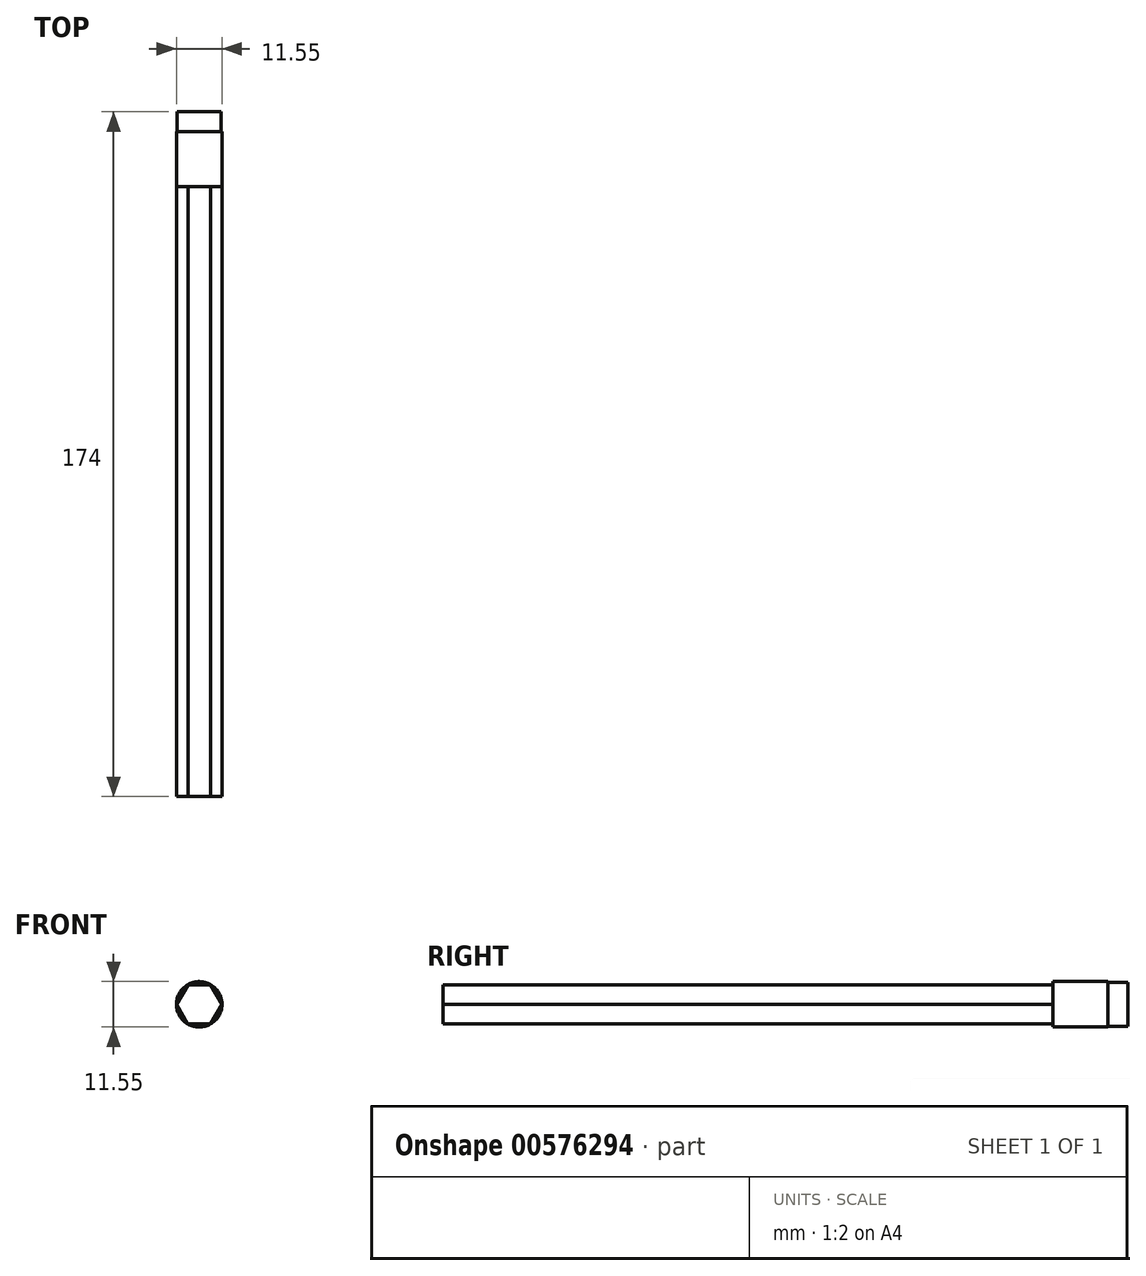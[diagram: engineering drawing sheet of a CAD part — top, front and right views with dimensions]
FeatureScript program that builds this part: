
annotation { "Feature Type Name" : "Feature", "Feature Type Description" : "" }
export const myFeature = defineFeature(function(context is Context, id is Id, definition is map)
    precondition{}
    {
        {
            var Q0;
            Q0=qCreatedBy(makeId("Front.planeOp"),FACE);
            var sketch = newSketch(context, id + "F0", { "sketchPlane" : qUnion([Q0])});
            skCircle(sketch, "E0.cCircle", {"center": v(-29.57, 29.31) * mm, "radius": 5 * mm, "construction": true});
            skLineSegment(sketch, "E0.0", {"start": v(-26.68, 34.31) * mm, "end": v(-23.8, 29.31) * mm});
            skLineSegment(sketch, "E0.1", {"start": v(-23.8, 29.31) * mm, "end": v(-26.69, 24.31) * mm});
            skLineSegment(sketch, "E0.2", {"start": v(-26.69, 24.31) * mm, "end": v(-32.46, 24.31) * mm});
            skLineSegment(sketch, "E0.3", {"start": v(-32.46, 24.31) * mm, "end": v(-35.35, 29.31) * mm});
            skLineSegment(sketch, "E0.4", {"start": v(-35.35, 29.31) * mm, "end": v(-32.46, 34.31) * mm});
            skLineSegment(sketch, "E0.5", {"start": v(-32.46, 34.31) * mm, "end": v(-26.68, 34.31) * mm});
            skPoint(sketch, "E0.0.midPoint", {"position": v(-25.24, 31.81) * mm});
            skSolve(sketch);
        }
        {
            var Q0;
            Q0 = qSketchRegion(id + "F0", true);
            extrude(context, id + "F1", {"entities" : qUnion([Q0]), "depth" : 155 * mm, "offsetDistance" : 25 * mm});
        }
        {
            var Q0;
            Q0=makeQuery(id+"F1.opExtrude","CAP_FACE",FACE,{"disambiguationData":[OSD([sQuery(id+"F0.wireOp",EDGE,"E0.0"),sQuery(id+"F0.wireOp",EDGE,"E0.1"),sQuery(id+"F0.wireOp",EDGE,"E0.2"),sQuery(id+"F0.wireOp",EDGE,"E0.3"),sQuery(id+"F0.wireOp",EDGE,"E0.4"),sQuery(id+"F0.wireOp",EDGE,"E0.5")])],"isStart":true});
            var sketch = newSketch(context, id + "F2", { "sketchPlane" : qUnion([Q0])});
            skCircle(sketch, "E1", {"center": v(29.57, 29.31) * mm, "radius": 5.77 * mm});
            skPoint(sketch, "E1.centerSnap0", {"position": v(29.57, 34.31) * mm});
            skSolve(sketch);
        }
        {
            var Q0;
            Q0 = qSketchRegion(id + "F2", true);
            extrude(context, id + "F3", {"entities" : qUnion([Q0]), "depth" : 14 * mm, "offsetDistance" : 25 * mm});
        }
        {
            var Q0;
            Q0=makeQuery(id+"F3.opExtrude","CAP_FACE",FACE,{"disambiguationData":[OSD([sQuery(id+"F2.wireOp",EDGE,"E1")])],"isStart":false});
            var sketch = newSketch(context, id + "F4", { "sketchPlane" : qUnion([Q0])});
            skCircle(sketch, "E2", {"center": v(29.57, 29.31) * mm, "radius": 5.6 * mm});
            skSolve(sketch);
        }
        {
            var Q0;
            Q0 = qSketchRegion(id + "F4", true);
            extrude(context, id + "F5", {"entities" : qUnion([Q0]), "depth" : 5 * mm, "offsetDistance" : 25 * mm});
        }
    });
